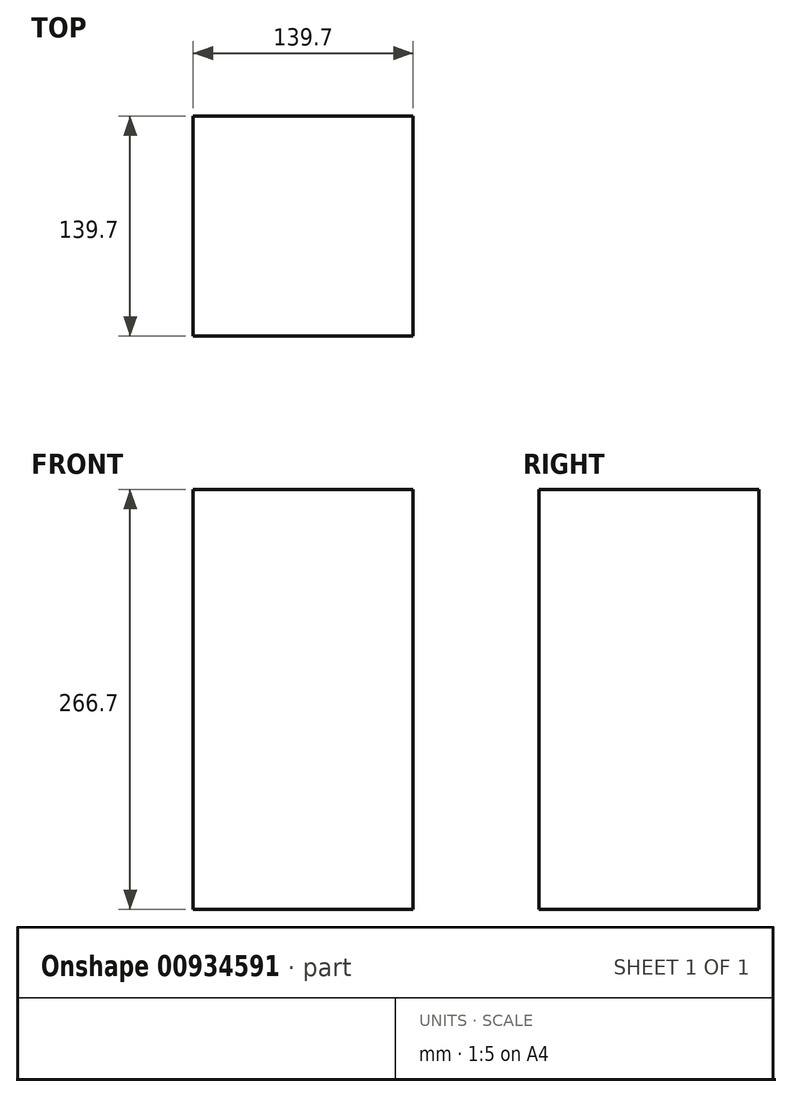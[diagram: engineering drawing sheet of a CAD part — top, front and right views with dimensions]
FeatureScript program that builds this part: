
annotation { "Feature Type Name" : "Feature", "Feature Type Description" : "" }
export const myFeature = defineFeature(function(context is Context, id is Id, definition is map)
    precondition{}
    {
        {
            var Q0;
            Q0=qCreatedBy(makeId("Top.planeOp"),FACE);
            var sketch = newSketch(context, id + "F0", { "sketchPlane" : qUnion([Q0])});
            skLineSegment(sketch, "E0.bottom", {"start": v(-169.45, 345.9) * mm, "end": v(-309.15, 345.9) * mm});
            skLineSegment(sketch, "E0.top", {"start": v(-169.45, 206.2) * mm, "end": v(-309.15, 206.2) * mm});
            skLineSegment(sketch, "E0.left", {"start": v(-169.45, 345.9) * mm, "end": v(-169.45, 206.2) * mm});
            skLineSegment(sketch, "E0.right", {"start": v(-309.15, 345.9) * mm, "end": v(-309.15, 206.2) * mm});
            skSolve(sketch);
        }
        {
            var Q0;
            Q0=makeQuery(id+"F0.imprint","IMPRINT",FACE,{"disambiguationData":[TD([[makeQuery(id+"F0.imprint","IMPRINT",EDGE,{"derivedFrom":sQuery(id+"F0.wireOp",EDGE,"E0.bottom")}),1.0]])]});
            extrude(context, id + "F1", {"entities" : qUnion([Q0]), "oppositeDirection" : true, "depth" : 266.7 * mm, "offsetDistance" : 25.4 * mm});
        }
    });
